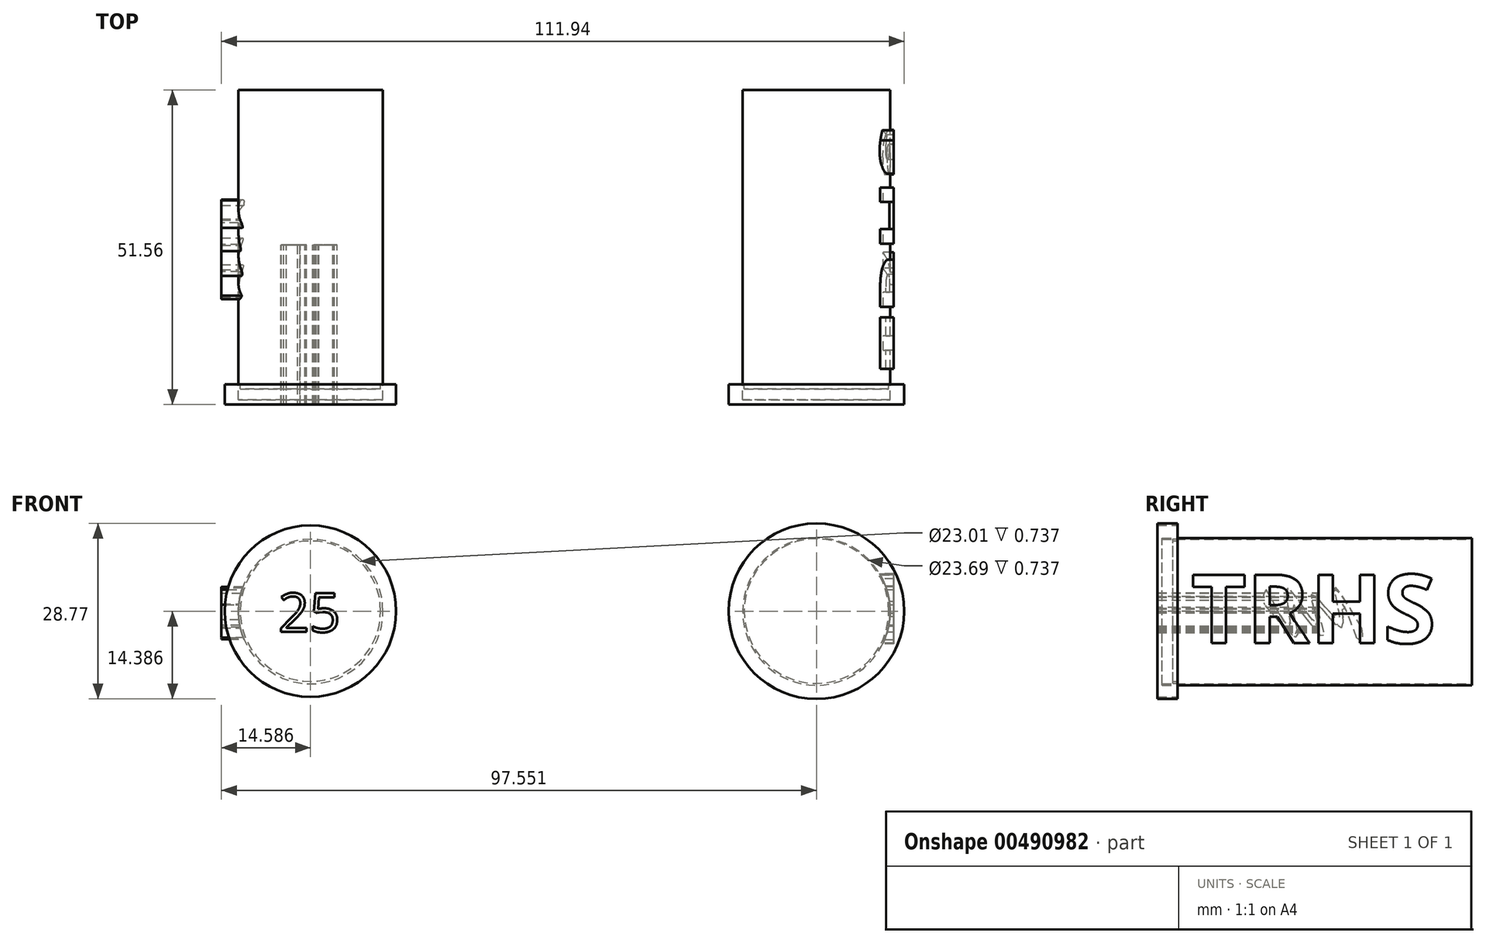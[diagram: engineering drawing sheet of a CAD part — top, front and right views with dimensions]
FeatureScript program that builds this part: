
annotation { "Feature Type Name" : "Feature", "Feature Type Description" : "" }
export const myFeature = defineFeature(function(context is Context, id is Id, definition is map)
    precondition{}
    {
        {
            var Q0;
            Q0=qCreatedBy(makeId("Front.planeOp"),FACE);
            var sketch = newSketch(context, id + "F0", { "sketchPlane" : qUnion([Q0])});
            skCircle(sketch, "E0", {"center": v(-42.26, 34.84) * mm, "radius": 11.85 * mm});
            skCircle(sketch, "E1", {"center": v(40.65, 34.84) * mm, "radius": 12.08 * mm});
            skSolve(sketch);
        }
        {
            var Q0;
            Q0=makeQuery(id+"F0.imprint","IMPRINT",FACE,{"disambiguationData":[TD([[makeQuery(id+"F0.imprint","IMPRINT",EDGE,{"derivedFrom":sQuery(id+"F0.wireOp",EDGE,"E1")}),1.0]])]});
            var Q1;
            Q1=makeQuery(id+"F0.imprint","IMPRINT",FACE,{"disambiguationData":[TD([[makeQuery(id+"F0.imprint","IMPRINT",EDGE,{"derivedFrom":sQuery(id+"F0.wireOp",EDGE,"E0")}),1.0]])]});
            extrude(context, id + "F1", {"entities" : qUnion([Q0, Q1]), "depth" : 25.4 * mm, "hasSecondDirection" : true, "secondDirectionOppositeDirection" : true, "secondDirectionDepth" : 25.4 * mm});
        }
        {
            var Q0;
            Q0=qCreatedBy(makeId("Right.planeOp"),FACE);
            var sketch = newSketch(context, id + "F2", { "sketchPlane" : qUnion([Q0])});
            skText(sketch, "E2", { "text": "TRHS", "fontName": "OpenSans-Bold.ttf"});
            const initialGuessF2  = {"E2": [-0.02065, 0.02968, 1, 0, 0.0113]};
            skSetInitialGuess(sketch, initialGuessF2);
            skSolve(sketch);
        }
        {
            var Q0;
            Q0 = qSketchRegion(id + "F2", true);
            extrude(context, id + "F3", {"entities" : qUnion([Q0]), "operationType" : NewBodyOperationType.ADD, "depth" : 53.34 * mm, "hasSecondDirection" : true, "secondDirectionOppositeDirection" : false, "secondDirectionDepth" : 39.62 * mm});
        }
        {
            var Q0;
            Q0=qCreatedBy(makeId("Right.planeOp"),FACE);
            var sketch = newSketch(context, id + "F4", { "sketchPlane" : qUnion([Q0])});
            skFitSpline(sketch, "E3", {"points": [v(7.28, 32.17) * mm, v(2.79, 38.67) * mm, v(3.46, 33.51) * mm, v(-0.91, 37.78) * mm, v(0, 32.62) * mm, v(-4.84, 38.67) * mm, v(-4.4, 32.5) * mm, v(-8.32, 38.45) * mm], "startDerivative": vector(-42.11, 72.46) * mm, "endDerivative": vector(-37.75, 70.72) * mm});
            skFitSpline(sketch, "E4", {"points": [v(6.5, 30.46) * mm, v(4.08, 35.98) * mm, v(3.92, 32.17) * mm, v(0, 35.98) * mm, v(1.07, 30.67) * mm, v(-3.93, 35.98) * mm, v(-3.22, 30.83) * mm, v(-8.61, 35.98) * mm], "startDerivative": vector(-20.4, 60.36) * mm, "endDerivative": vector(-48.12, 53.48) * mm});
            skFitSpline(sketch, "E5", {"points": [v(7.28, 32.17) * mm, v(7.28, 30.35) * mm, v(6.5, 30.46) * mm], "startDerivative": vector(0.6, -4.01) * mm, "endDerivative": vector(-2.37, 0.94) * mm});
            skFitSpline(sketch, "E6", {"points": [v(-8.32, 38.45) * mm, v(-8.61, 35.98) * mm], "startDerivative": vector(-1.83, -2.64) * mm, "endDerivative": vector(1.2, -2.86) * mm});
            skText(sketch, "E7", { "text": "25\n", "fontName": "OpenSans-Regular.ttf"});
            const initialGuessF4  = {"E7": [0.01433, 0.03295, 1, 0, 0.0034]};
            skSetInitialGuess(sketch, initialGuessF4);
            skSolve(sketch);
        }
        {
            var Q0;
            Q0=makeQuery(id+"F4.imprint","IMPRINT",FACE,{"disambiguationData":[TD([[makeQuery(id+"F4.imprint","IMPRINT",EDGE,{"derivedFrom":sQuery(id+"F4.wireOp",EDGE,"E3")}),1.0]])]});
            extrude(context, id + "F5", {"entities" : qUnion([Q0]), "operationType" : NewBodyOperationType.ADD, "oppositeDirection" : true, "depth" : 56.9 * mm, "hasSecondDirection" : true, "secondDirectionOppositeDirection" : true, "secondDirectionDepth" : 50.04 * mm});
        }
        {
            var Q0;
            Q0=qCreatedBy(makeId("Front.planeOp"),FACE);
            var sketch = newSketch(context, id + "F6", { "sketchPlane" : qUnion([Q0])});
            skCircle(sketch, "E8", {"center": v(-42.31, 34.92) * mm, "radius": 14.05 * mm});
            skCircle(sketch, "E9", {"center": v(40.65, 34.92) * mm, "radius": 14.39 * mm});
            skSolve(sketch);
        }
        {
            var Q0;
            Q0 = qSketchRegion(id + "F6", true);
            extrude(context, id + "F7", {"entities" : qUnion([Q0]), "depth" : 26.16 * mm, "hasSecondDirection" : true, "secondDirectionOppositeDirection" : false, "secondDirectionDepth" : 22.9 * mm});
        }
        {
            var Q0;
            Q0=qCreatedBy(makeId("Front.planeOp"),FACE);
            var sketch = newSketch(context, id + "F8", { "sketchPlane" : qUnion([Q0])});
            skText(sketch, "E10", { "text": "25\n", "fontName": "OpenSans-Regular.ttf"});
            const initialGuessF8  = {"E10": [-0.04758, 0.0315, 1, 0, 0.00641]};
            skSetInitialGuess(sketch, initialGuessF8);
            skSolve(sketch);
        }
        {
            var Q0;
            Q0 = qSketchRegion(id + "F8", true);
            extrude(context, id + "F9", {"entities" : qUnion([Q0]), "depth" : 26.16 * mm});
        }
        {
            var Q0;
            Q0=makeQuery(id+"F7.opExtrude","CAP_FACE",FACE,{"disambiguationData":[OSD([sQuery(id+"F6.wireOp",EDGE,"E8")])],"isStart":true});
            var Q1;
            Q1=makeQuery(id+"F7.opExtrude","CAP_FACE",FACE,{"disambiguationData":[OSD([sQuery(id+"F6.wireOp",EDGE,"E9")])],"isStart":true});
            shell(context, id + "F10", {"entities" : qUnion([Q0, Q1]), "thickness" : 2.54 * mm});
        }
    });
